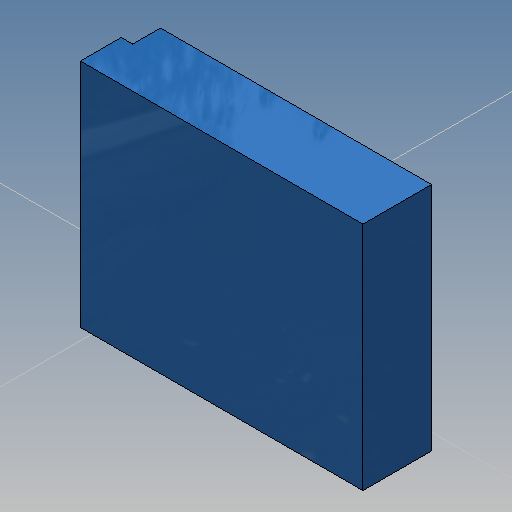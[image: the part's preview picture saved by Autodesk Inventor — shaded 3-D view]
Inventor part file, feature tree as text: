
AUTODESK INVENTOR PART (.ipt)
format: ipt  version: 2019 (Build 230136000, 136)  size: 129,024 bytes
history: native  units: in
note: dims shown in document units (in); Inventor stores cm internally (conversion verified against a paired STEP export)
features: extrude x2, sketch x2, other x2, plane x1
ambient origin geometry x8: Origin, YZ Plane, XZ Plane, XY Plane, X Axis, Y Axis, Z Axis, Center Point
bodies: Solid1 (feature_tree)
feature tree (7):
  extrude  "Extrusion1"  Depth=0.44in
  sketch  "Sketch2"  dims[d2=0.156in d3=0.0in d4=0.075in d5=0.2in d6=0.0in]
  plane  "Work Plane1"
  extrude  "Extrusion2"  Depth=0.075in
  other  "Move Face1"
  other  "Move Face2"
  sketch  "Sketch1"  dims[d0=0.498in d1=0.44in]
